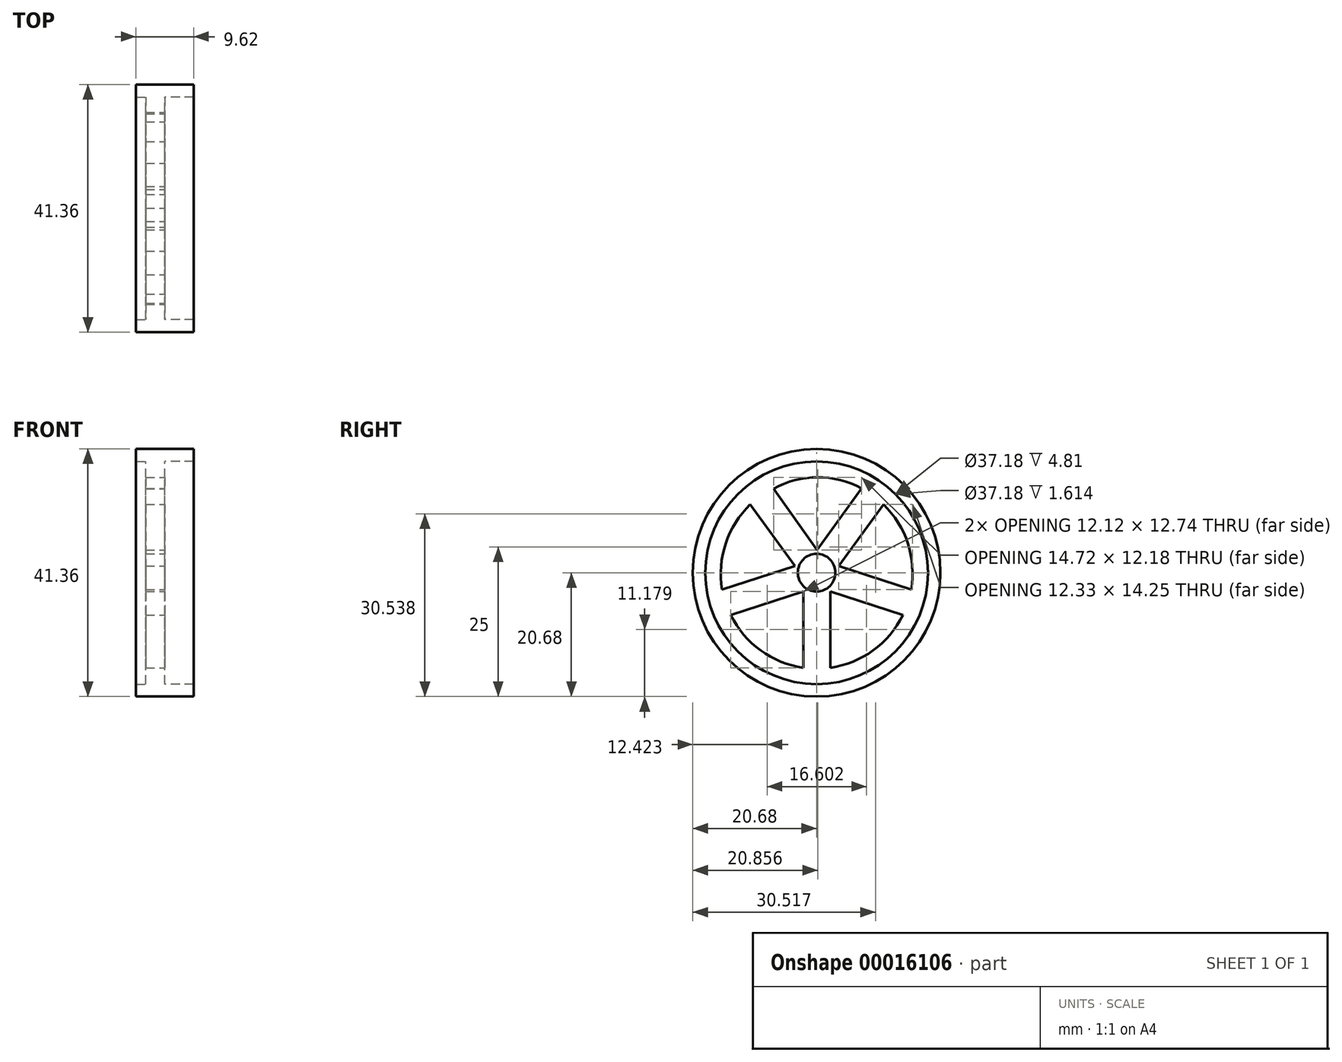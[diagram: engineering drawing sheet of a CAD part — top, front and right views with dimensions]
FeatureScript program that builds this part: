
annotation { "Feature Type Name" : "Feature", "Feature Type Description" : "" }
export const myFeature = defineFeature(function(context is Context, id is Id, definition is map)
    precondition{}
    {
        {
            var Q0;
            Q0=qCreatedBy(makeId("Right.planeOp"),FACE);
            var sketch = newSketch(context, id + "F0", { "sketchPlane" : qUnion([Q0])});
            skCircle(sketch, "E0", {"center": v(0, 0) * mm, "radius": 20.68 * mm});
            skPoint(sketch, "E1.0.midPoint", {"position": v(0.04, -3.13) * mm});
            skLineSegment(sketch, "E2", {"start": v(2.29, -3.13) * mm, "end": v(14.4, -7.07) * mm});
            skLineSegment(sketch, "E3", {"start": v(3.67, 1.13) * mm, "end": v(15.8, -2.8) * mm});
            skLineSegment(sketch, "E4", {"start": v(3.67, 1.13) * mm, "end": v(11.16, 11.44) * mm});
            skLineSegment(sketch, "E5", {"start": v(0.04, 3.77) * mm, "end": v(7.53, 14.08) * mm});
            skLineSegment(sketch, "E6", {"start": v(-3.58, 1.13) * mm, "end": v(-11.07, 11.44) * mm});
            skLineSegment(sketch, "E7", {"start": v(0.04, 3.77) * mm, "end": v(-7.18, 14.03) * mm});
            skLineSegment(sketch, "E8", {"start": v(-3.58, 1.13) * mm, "end": v(-15.82, -2.8) * mm});
            skLineSegment(sketch, "E9", {"start": v(-2.2, -3.13) * mm, "end": v(-14.32, -7.07) * mm});
            skLineSegment(sketch, "E10", {"start": v(-2.2, -3.13) * mm, "end": v(-2.2, -15.87) * mm});
            skLineSegment(sketch, "E11", {"start": v(2.29, -3.13) * mm, "end": v(2.29, -15.87) * mm});
            skArc(sketch, "E12", {"start": v(15.8, -2.8) * mm, "mid": v(15.23, 4.9) * mm, "end": v(11.16, 11.44) * mm});
            skArc(sketch, "E13", {"start": v(2.29, -15.87) * mm, "mid": v(9.44, -12.97) * mm, "end": v(14.4, -7.07) * mm});
            skArc(sketch, "E14", {"start": v(-14.32, -7.07) * mm, "mid": v(-9.34, -12.97) * mm, "end": v(-2.2, -15.87) * mm});
            skArc(sketch, "E15", {"start": v(-11.07, 11.44) * mm, "mid": v(-15.17, 4.9) * mm, "end": v(-15.82, -2.8) * mm});
            skArc(sketch, "E16", {"start": v(7.53, 14.08) * mm, "mid": v(0.17, 15.95) * mm, "end": v(-7.18, 14.03) * mm});
            skCircle(sketch, "E17", {"center": v(0, 0.01) * mm, "radius": 3.14 * mm});
            skCircle(sketch, "E18", {"center": v(0, 0) * mm, "radius": 18.59 * mm});
            skSolve(sketch);
        }
        {
            var Q0;
            Q0=makeQuery(id+"F0.imprint","IMPRINT",FACE,{"disambiguationData":[TD([[makeQuery(id+"F0.imprint","IMPRINT",EDGE,{"derivedFrom":sQuery(id+"F0.wireOp",EDGE,"E0")}),1.0]])]});
            extrude(context, id + "F1", {"entities" : qUnion([Q0]), "depth" : 4.8 * mm});
        }
        {
            var Q0;
            Q0=makeQuery(id+"F0.imprint","IMPRINT",FACE,{"disambiguationData":[TD([[makeQuery(id+"F0.imprint","IMPRINT",EDGE,{"derivedFrom":sQuery(id+"F0.wireOp",EDGE,"E2")}),1.0]])]});
            extrude(context, id + "F2", {"entities" : qUnion([Q0]), "operationType" : NewBodyOperationType.ADD, "oppositeDirection" : true, "depth" : 3.2 * mm});
        }
        {
            var Q0;
            Q0=makeQuery(id+"F0.imprint","IMPRINT",FACE,{"disambiguationData":[TD([[makeQuery(id+"F0.imprint","IMPRINT",EDGE,{"derivedFrom":sQuery(id+"F0.wireOp",EDGE,"E0")}),1.0]])]});
            extrude(context, id + "F3", {"entities" : qUnion([Q0]), "operationType" : NewBodyOperationType.ADD, "oppositeDirection" : true, "depth" : 4.8 * mm});
        }
    });
